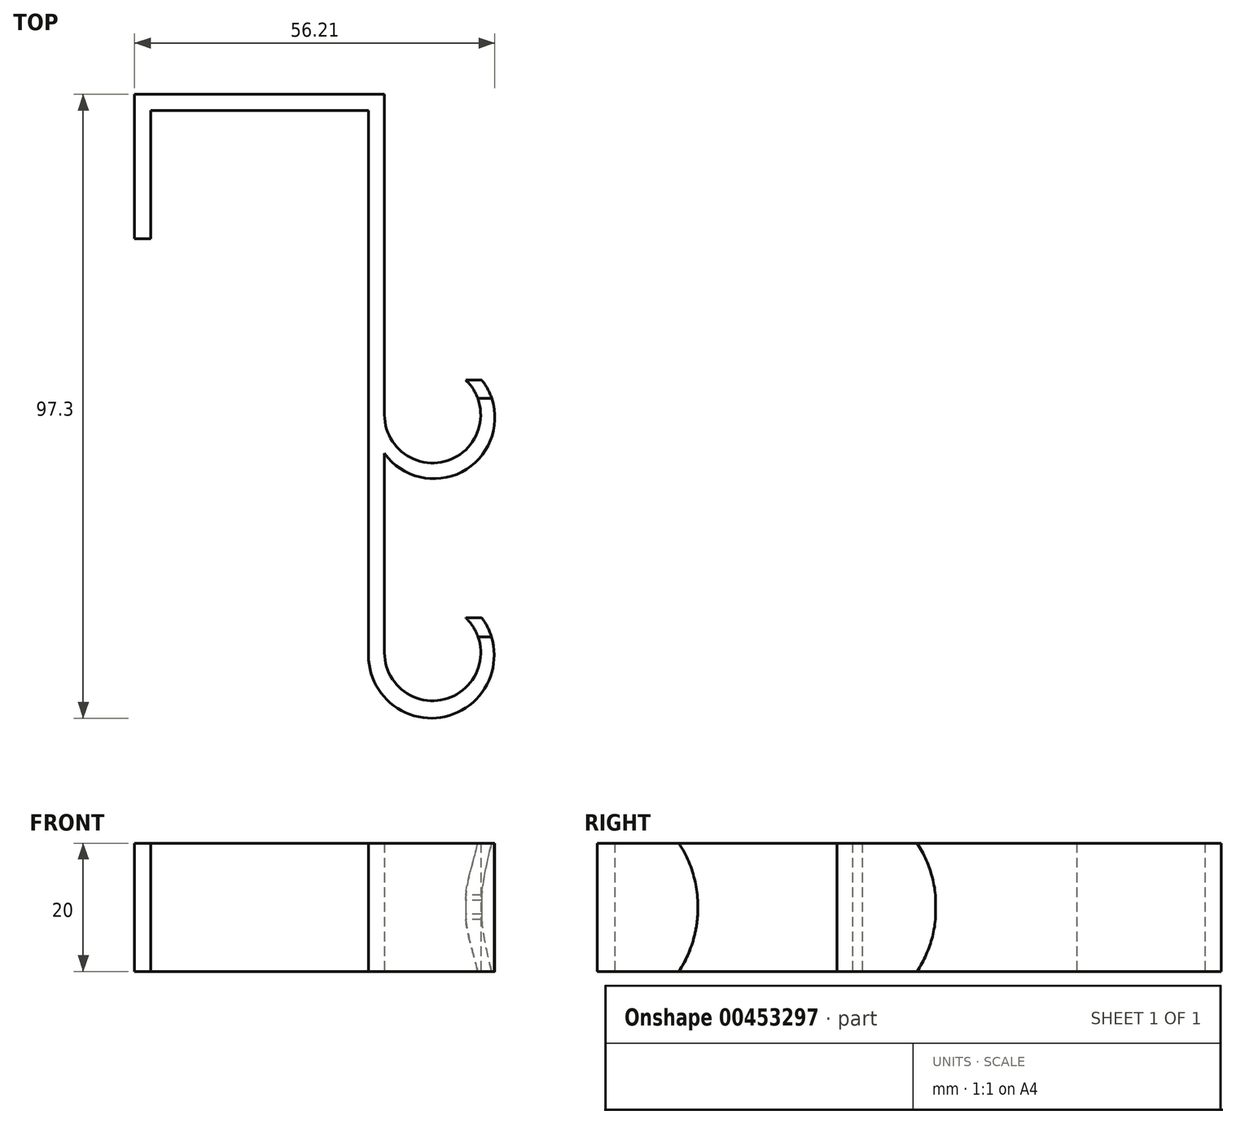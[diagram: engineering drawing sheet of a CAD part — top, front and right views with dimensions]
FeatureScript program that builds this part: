
annotation { "Feature Type Name" : "Feature", "Feature Type Description" : "" }
export const myFeature = defineFeature(function(context is Context, id is Id, definition is map)
    precondition{}
    {
        {
            var Q0;
            Q0=qCreatedBy(makeId("Top.planeOp"),FACE);
            var sketch = newSketch(context, id + "F0", { "sketchPlane" : qUnion([Q0])});
            skLineSegment(sketch, "E0", {"start": v(-41.78, 54.77) * mm, "end": v(-41.78, 74.77) * mm});
            skLineSegment(sketch, "E1", {"start": v(-41.78, 74.77) * mm, "end": v(-7.78, 74.77) * mm});
            skLineSegment(sketch, "E2", {"start": v(-7.78, 74.77) * mm, "end": v(-7.78, -10.23) * mm});
            skLineSegment(sketch, "E3", {"start": v(-41.78, 54.77) * mm, "end": v(-44.28, 54.77) * mm});
            skLineSegment(sketch, "E4", {"start": v(-44.28, 54.77) * mm, "end": v(-44.28, 77.27) * mm});
            skLineSegment(sketch, "E5", {"start": v(-44.28, 77.27) * mm, "end": v(-5.28, 77.27) * mm});
            skLineSegment(sketch, "E6", {"start": v(-5.28, 77.27) * mm, "end": v(-5.28, 27.27) * mm});
            skArc(sketch, "E7", {"start": v(-5.28, 27.27) * mm, "mid": v(5.18, 20.38) * mm, "end": v(7.38, 32.7) * mm});
            skArc(sketch, "E8", {"start": v(-5.28, 21.27) * mm, "mid": v(8.15, 19.23) * mm, "end": v(9.88, 32.7) * mm});
            skLineSegment(sketch, "E9", {"start": v(-5.28, 21.27) * mm, "end": v(-5.28, -9.82) * mm});
            skArc(sketch, "E10", {"start": v(-5.28, -9.82) * mm, "mid": v(5.18, -16.71) * mm, "end": v(7.38, -4.38) * mm});
            skArc(sketch, "E11", {"start": v(-7.78, -10.23) * mm, "mid": v(5.1, -19.53) * mm, "end": v(9.88, -4.38) * mm});
            skLineSegment(sketch, "E12", {"start": v(7.38, -4.38) * mm, "end": v(9.88, -4.38) * mm});
            skLineSegment(sketch, "E13", {"start": v(7.38, 32.7) * mm, "end": v(9.88, 32.7) * mm});
            skSolve(sketch);
        }
        {
            var Q0;
            Q0 = qSketchRegion(id + "F0", true);
            extrude(context, id + "F1", {"entities" : qUnion([Q0]), "depth" : 20 * mm});
        }
        {
            var Q0;
            Q0=qCreatedBy(makeId("Right.planeOp"),FACE);
            var sketch = newSketch(context, id + "F2", { "sketchPlane" : qUnion([Q0])});
            skArc(sketch, "E14", {"start": v(29.83, 0) * mm, "mid": v(32.8, 10) * mm, "end": v(29.83, 20) * mm});
            skLineSegment(sketch, "E15", {"start": v(29.83, 20) * mm, "end": v(34.95, 20) * mm});
            skLineSegment(sketch, "E16", {"start": v(34.95, 20) * mm, "end": v(34.95, 0) * mm});
            skLineSegment(sketch, "E17", {"start": v(34.95, 0) * mm, "end": v(29.83, 0) * mm});
            skArc(sketch, "E18", {"start": v(-7.33, 0) * mm, "mid": v(-4.35, 10) * mm, "end": v(-7.33, 20) * mm});
            skLineSegment(sketch, "E19", {"start": v(-7.33, 20) * mm, "end": v(-2.22, 20) * mm});
            skLineSegment(sketch, "E20", {"start": v(-2.22, 20) * mm, "end": v(-2.22, 0) * mm});
            skLineSegment(sketch, "E21", {"start": v(-2.22, 0) * mm, "end": v(-7.33, 0) * mm});
            skSolve(sketch);
        }
        {
            var Q0;
            Q0 = qSketchRegion(id + "F2", true);
            extrude(context, id + "F3", {"entities" : qUnion([Q0]), "operationType" : NewBodyOperationType.REMOVE, "depth" : 25 * mm});
        }
    });
